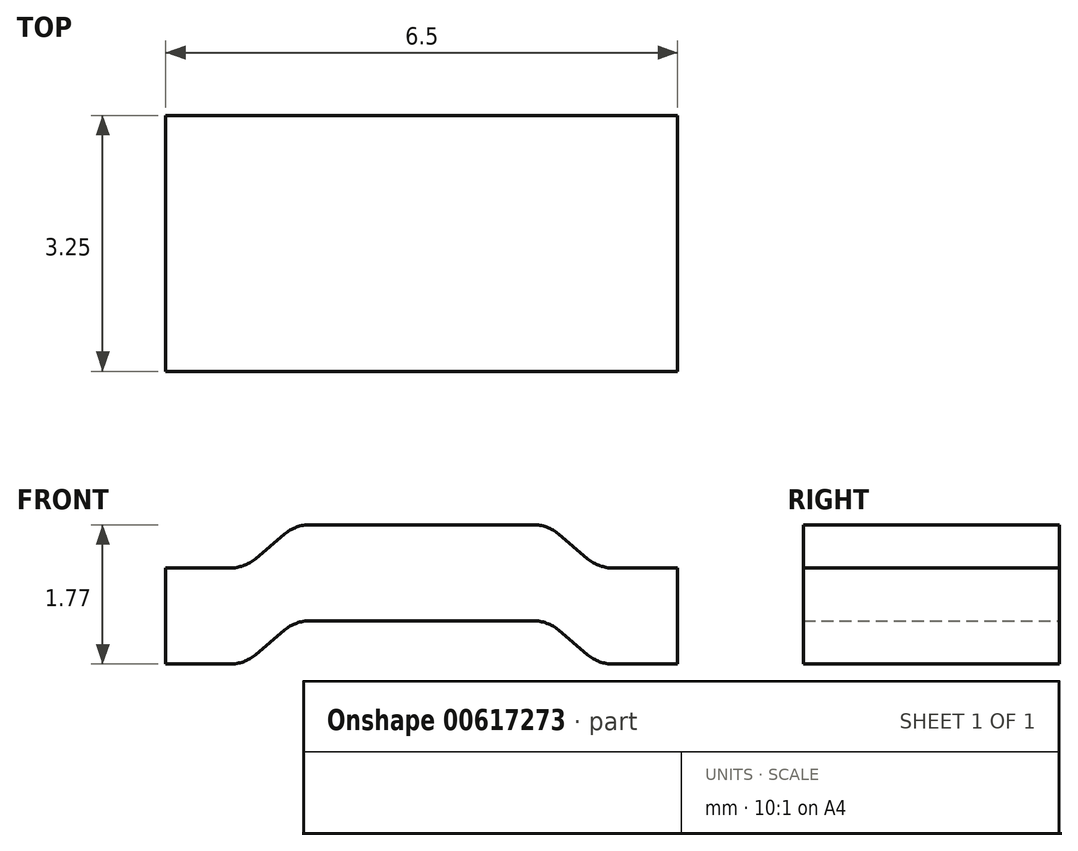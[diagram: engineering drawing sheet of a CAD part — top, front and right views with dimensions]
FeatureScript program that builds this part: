
annotation { "Feature Type Name" : "Feature", "Feature Type Description" : "" }
export const myFeature = defineFeature(function(context is Context, id is Id, definition is map)
    precondition{}
    {
        {
            var Q0;
            Q0=qCreatedBy(makeId("Front.planeOp"),FACE);
            var sketch = newSketch(context, id + "F0", { "sketchPlane" : qUnion([Q0])});
            skLineSegment(sketch, "E0", {"start": v(0, 0) * mm, "end": v(0, 1.22) * mm});
            skLineSegment(sketch, "E1", {"start": v(0, 1.22) * mm, "end": v(1, 1.22) * mm});
            skLineSegment(sketch, "E2", {"start": v(1, 1.22) * mm, "end": v(1.65, 1.77) * mm});
            skLineSegment(sketch, "E3", {"start": v(1.65, 1.77) * mm, "end": v(3.25, 1.77) * mm});
            skLineSegment(sketch, "E4", {"start": v(3.25, 1.77) * mm, "end": v(3.25, 0.55) * mm});
            skLineSegment(sketch, "E5", {"start": v(3.25, 0.55) * mm, "end": v(1.65, 0.55) * mm});
            skLineSegment(sketch, "E6", {"start": v(1.65, 0.55) * mm, "end": v(1, 0) * mm});
            skLineSegment(sketch, "E7", {"start": v(1, 0) * mm, "end": v(0, 0) * mm});
            skSolve(sketch);
        }
        {
            var Q0;
            Q0=makeQuery(id+"F0.imprint","IMPRINT",FACE,{"disambiguationData":[TD([[makeQuery(id+"F0.imprint","IMPRINT",EDGE,{"derivedFrom":sQuery(id+"F0.wireOp",EDGE,"E0")}),-1.0]])]});
            extrude(context, id + "F1", {"entities" : qUnion([Q0]), "depth" : 3.25 * mm, "offsetDistance" : 25 * mm});
        }
        {
            var Q0;
            Q0=makeQuery(id+"F1.opExtrude","SWEPT_EDGE",EDGE,{"disambiguationData":[OSD([sQuery(id+"F0.wireOp",EDGE,"E6"),sQuery(id+"F0.wireOp",EDGE,"E7")])]});
            var Q1;
            Q1=makeQuery(id+"F1.opExtrude","SWEPT_EDGE",EDGE,{"disambiguationData":[OSD([sQuery(id+"F0.wireOp",EDGE,"E5"),sQuery(id+"F0.wireOp",EDGE,"E6")])]});
            var Q2;
            Q2=makeQuery(id+"F1.opExtrude","SWEPT_EDGE",EDGE,{"disambiguationData":[OSD([sQuery(id+"F0.wireOp",EDGE,"E1"),sQuery(id+"F0.wireOp",EDGE,"E2")])]});
            var Q3;
            Q3=makeQuery(id+"F1.opExtrude","SWEPT_EDGE",EDGE,{"disambiguationData":[OSD([sQuery(id+"F0.wireOp",EDGE,"E2"),sQuery(id+"F0.wireOp",EDGE,"E3")])]});
            fillet(context, id + "F2", {"entities" : qUnion([Q0, Q1, Q2, Q3]), "radius" : .5 * mm, "tangentPropagation" : true, "allowEdgeOverflow" : false});
        }
        {
            var Q0;
            Q0=makeQuery(id+"F1.opExtrude","SWEPT_BODY",BODY,{"disambiguationData":[OSD([sQuery(id+"F0.wireOp",EDGE,"E0"),sQuery(id+"F0.wireOp",EDGE,"E1"),sQuery(id+"F0.wireOp",EDGE,"E2"),sQuery(id+"F0.wireOp",EDGE,"E3"),sQuery(id+"F0.wireOp",EDGE,"E4"),sQuery(id+"F0.wireOp",EDGE,"E5"),sQuery(id+"F0.wireOp",EDGE,"E6"),sQuery(id+"F0.wireOp",EDGE,"E7")])]});
            var Q1;
            Q1=makeQuery(id+"F1.opExtrude","SWEPT_FACE",FACE,{"disambiguationData":[OSD([sQuery(id+"F0.wireOp",EDGE,"E4")])]});
            mirror(context, id + "F3", {"operationType" : NewBodyOperationType.ADD, "entities" : qUnion([Q0]), "mirrorPlane" : qUnion([Q1])});
        }
    });
